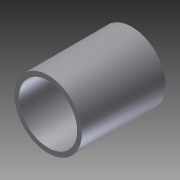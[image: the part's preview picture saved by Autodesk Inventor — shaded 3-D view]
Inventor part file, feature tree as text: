
AUTODESK INVENTOR PART (.ipt)
format: ipt  version: 2013 (Build 170138000, 138)  size: 84,992 bytes
history: native  units: in
note: dims shown in document units (in); Inventor stores cm internally (conversion verified against a paired STEP export)
features: extrude x1, sketch x1
ambient origin geometry x8: Origin, YZ Plane, XZ Plane, XY Plane, X Axis, Y Axis, Z Axis, Center Point
bodies: Solid1 (feature_tree)
feature tree (2):
  extrude  "Extrusion1"  Depth=1.25in
  sketch  "Sketch1"  dims[d0=1.45in d1=1.25in d2=1.8in d3=0.0in]
